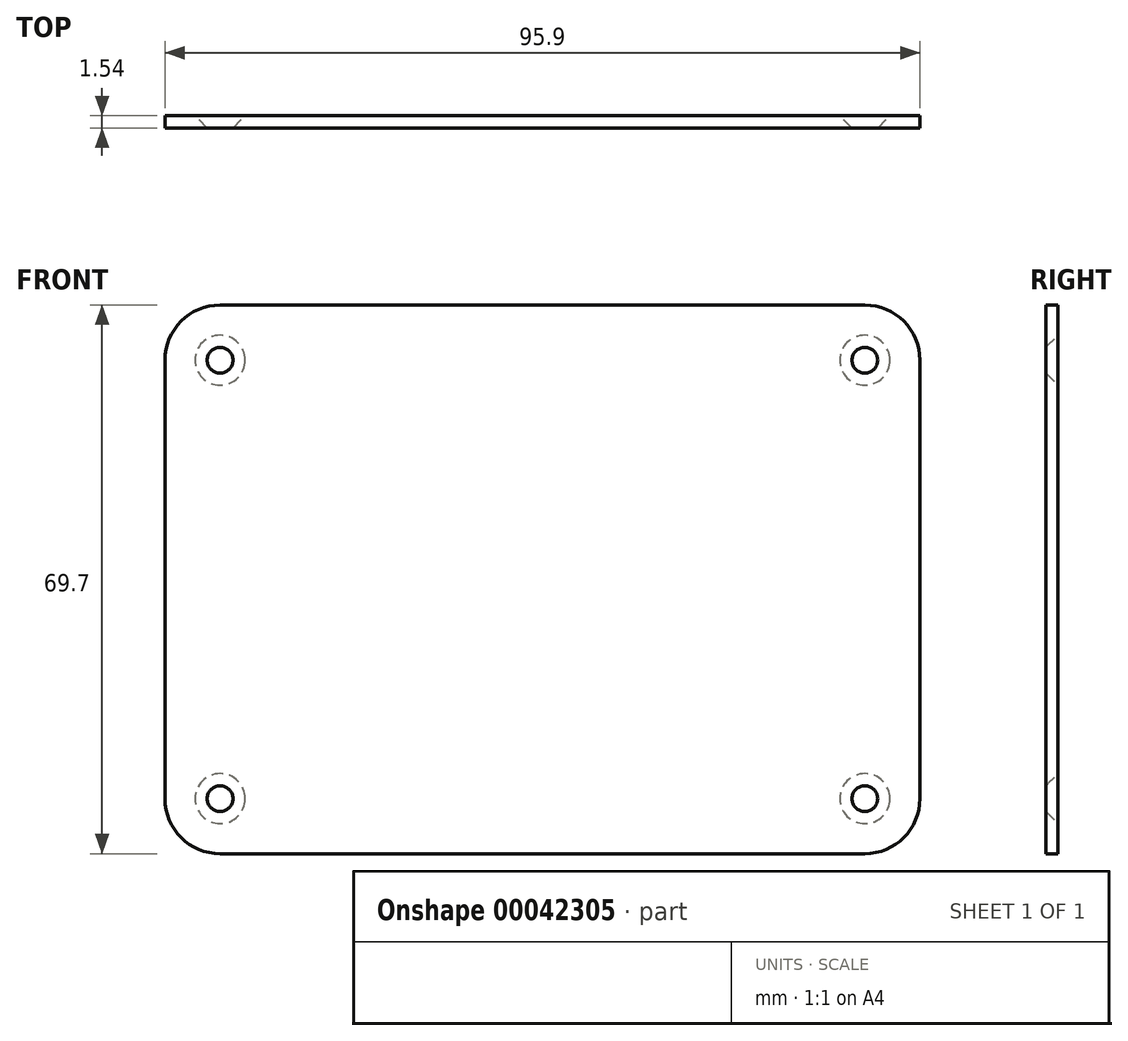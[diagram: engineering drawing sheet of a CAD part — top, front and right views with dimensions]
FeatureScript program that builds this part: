
annotation { "Feature Type Name" : "Feature", "Feature Type Description" : "" }
export const myFeature = defineFeature(function(context is Context, id is Id, definition is map)
    precondition{}
    {
        {
            var Q0;
            Q0=qCreatedBy(makeId("Front.planeOp"),FACE);
            var sketch = newSketch(context, id + "F0", { "sketchPlane" : qUnion([Q0])});
            skLineSegment(sketch, "E0.bottom", {"start": v(-56.34, 53.4) * mm, "end": v(39.56, 53.4) * mm});
            skLineSegment(sketch, "E0.top", {"start": v(-56.34, -16.3) * mm, "end": v(39.56, -16.3) * mm});
            skLineSegment(sketch, "E0.left", {"start": v(-56.34, 53.4) * mm, "end": v(-56.34, -16.3) * mm});
            skLineSegment(sketch, "E0.right", {"start": v(39.56, 53.4) * mm, "end": v(39.56, -16.3) * mm});
            skPoint(sketch, "E1", {"position": v(-49.34, 46.4) * mm});
            skPoint(sketch, "E2", {"position": v(32.56, 46.4) * mm});
            skPoint(sketch, "E3", {"position": v(32.56, -9.3) * mm});
            skPoint(sketch, "E4", {"position": v(-49.34, -9.3) * mm});
            skSolve(sketch);
        }
        {
            var Q0;
            Q0=makeQuery(id+"F0.imprint","IMPRINT",FACE,{"disambiguationData":[TD([[makeQuery(id+"F0.imprint","IMPRINT",EDGE,{"derivedFrom":sQuery(id+"F0.wireOp",EDGE,"E0.bottom")}),-1.0]])]});
            extrude(context, id + "F1", {"entities" : qUnion([Q0]), "depth" : 1.54 * mm});
        }
        {
            var Q0;
            Q0=makeQuery(id+"F1.opExtrude","SWEPT_EDGE",EDGE,{"disambiguationData":[OSD([sQuery(id+"F0.wireOp",EDGE,"E0.top"),sQuery(id+"F0.wireOp",EDGE,"E0.left")])]});
            var Q1;
            Q1=makeQuery(id+"F1.opExtrude","SWEPT_EDGE",EDGE,{"disambiguationData":[OSD([sQuery(id+"F0.wireOp",EDGE,"E0.top"),sQuery(id+"F0.wireOp",EDGE,"E0.right")])]});
            var Q2;
            Q2=makeQuery(id+"F1.opExtrude","SWEPT_EDGE",EDGE,{"disambiguationData":[OSD([sQuery(id+"F0.wireOp",EDGE,"E0.bottom"),sQuery(id+"F0.wireOp",EDGE,"E0.right")])]});
            var Q3;
            Q3=makeQuery(id+"F1.opExtrude","SWEPT_EDGE",EDGE,{"disambiguationData":[OSD([sQuery(id+"F0.wireOp",EDGE,"E0.bottom"),sQuery(id+"F0.wireOp",EDGE,"E0.left")])]});
            fillet(context, id + "F2", {"entities" : qUnion([Q0, Q1, Q2, Q3]), "radius" : 7 * mm, "tangentPropagation" : true, "allowEdgeOverflow" : false});
        }
        {
            var Q0;
            Q0=sQuery(id+"F0.wireOp",VERTEX,"E1");
            var Q1;
            Q1=sQuery(id+"F0.wireOp",VERTEX,"E2");
            var Q2;
            Q2=sQuery(id+"F0.wireOp",VERTEX,"E3");
            var Q3;
            Q3=sQuery(id+"F0.wireOp",VERTEX,"E4");
            var Q4;
            Q4=makeQuery(id+"F1.opExtrude","SWEPT_BODY",BODY,{"disambiguationData":[OSD([sQuery(id+"F0.wireOp",EDGE,"E0.bottom"),sQuery(id+"F0.wireOp",EDGE,"E0.top"),sQuery(id+"F0.wireOp",EDGE,"E0.left"),sQuery(id+"F0.wireOp",EDGE,"E0.right")])]});
            hole(context, id + "F3", {"style" : HoleStyle.C_SINK, "holeDiameter" : 2.84 * mm, "cSinkDiameter" : 6.35 * mm, "endStyle" : HoleEndStyle.THROUGH, "oppositeDirection" : true, "locations" : qUnion([Q0, Q1, Q2, Q3]), "scope" : qUnion([Q4]), "cSinkAngle" : 90 * degree});
        }
    });
